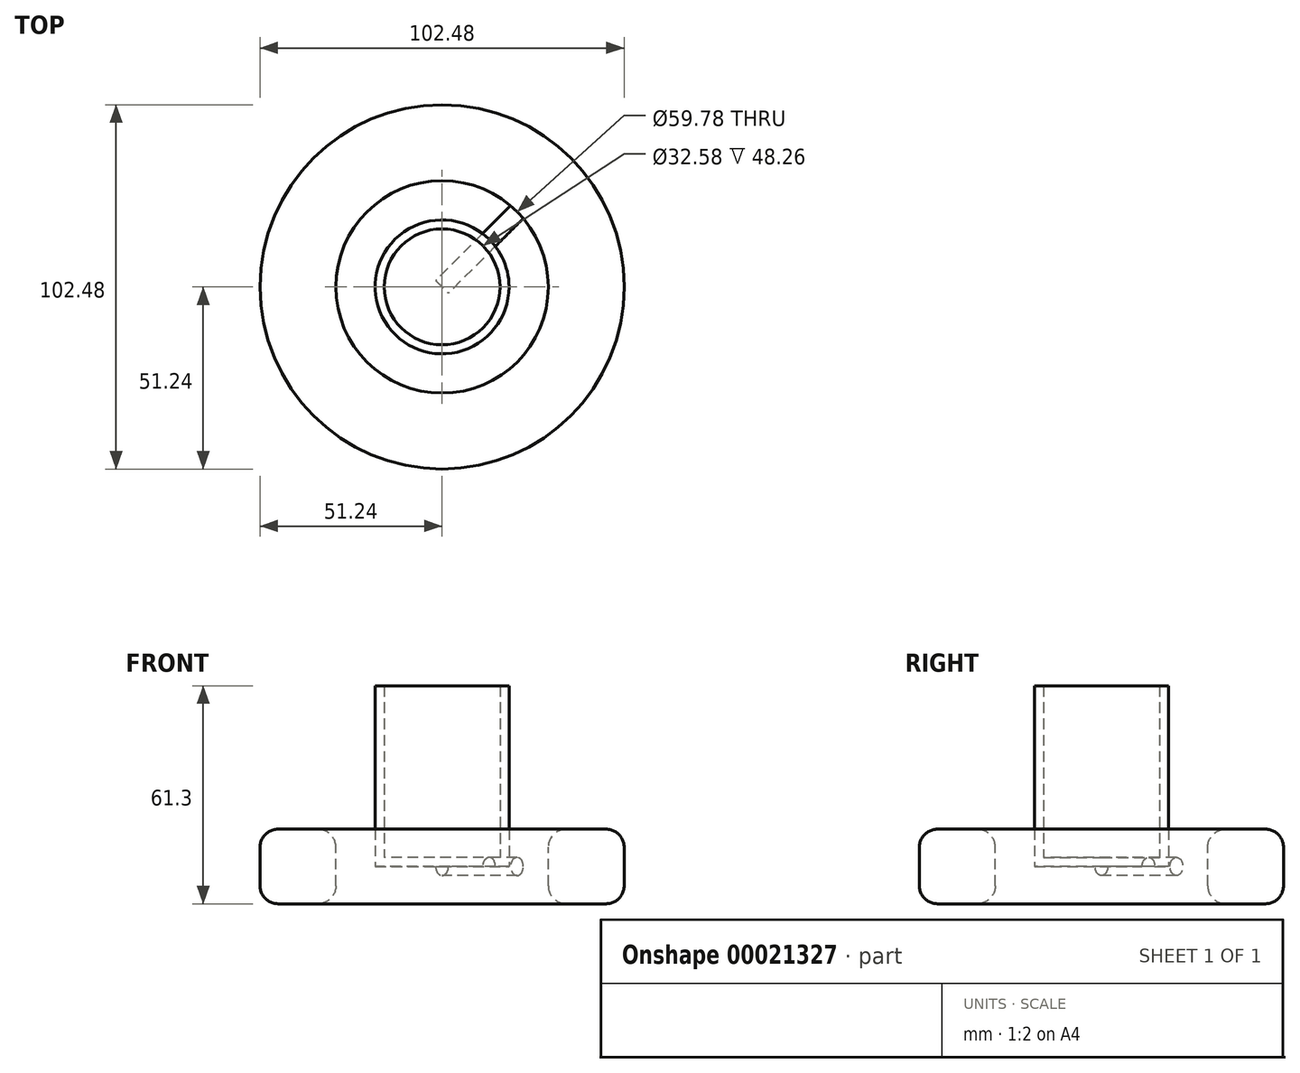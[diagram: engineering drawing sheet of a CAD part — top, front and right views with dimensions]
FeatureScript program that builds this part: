
annotation { "Feature Type Name" : "Feature", "Feature Type Description" : "" }
export const myFeature = defineFeature(function(context is Context, id is Id, definition is map)
    precondition{}
    {
        {
            var Q0;
            Q0=qCreatedBy(makeId("Front.planeOp"),FACE);
            var Q1;
            Q1=qCreatedBy(makeId("Right.planeOp"),FACE);
            cPlane(context, id + "F0", {"entities" : qUnion([Q0, Q1]), "cplaneType" : CPlaneType.MID_PLANE, "offset" : 152.4 * mm, "width" : 152.4 * mm, "height" : 152.4 * mm});
        }
        {
            var Q0;
            Q0=qCreatedBy(makeId("Front.planeOp"),FACE);
            var sketch = newSketch(context, id + "F1", { "sketchPlane" : qUnion([Q0])});
            skLineSegment(sketch, "E0.rect.bottom", {"start": v(-29.89, -10.5) * mm, "end": v(-51.24, -10.5) * mm});
            skLineSegment(sketch, "E0.rect.top", {"start": v(-29.89, 10.5) * mm, "end": v(-51.24, 10.5) * mm});
            skLineSegment(sketch, "E0.rect.left", {"start": v(-29.89, -10.5) * mm, "end": v(-29.89, 10.5) * mm});
            skLineSegment(sketch, "E0.rect.right", {"start": v(-51.24, -10.5) * mm, "end": v(-51.24, 10.5) * mm});
            skPoint(sketch, "E0.rect.middle", {"position": v(-40.56, 0) * mm});
            skSolve(sketch);
        }
        {
            var Q0;
            Q0=qCreatedBy(makeId("Front.planeOp"),FACE);
            var sketch = newSketch(context, id + "F2", { "sketchPlane" : qUnion([Q0])});
            skLineSegment(sketch, "E1", {"start": v(0, 53.18) * mm, "end": v(0, -49.93) * mm});
            skSolve(sketch);
        }
        {
            var Q0;
            Q0=makeQuery(id+"F1.imprint","IMPRINT",FACE,{"disambiguationData":[TD([[makeQuery(id+"F1.imprint","IMPRINT",EDGE,{"derivedFrom":sQuery(id+"F1.wireOp",EDGE,"E0.rect.bottom")}),-1.0]])]});
            var Q1;
            Q1=sQuery(id+"F2.wireOp",EDGE,"E1");
            revolve(context, id + "F3", {"entities" : qUnion([Q0]), "axis" : qUnion([Q1]), "revolveType" : RevolveType.FULL});
        }
        {
            var Q0;
            Q0=makeQuery(id+"F3.opRevolve","SWEPT_FACE",FACE,{"disambiguationData":[OSD([sQuery(id+"F1.wireOp",EDGE,"E0.rect.top")])]});
            fillet(context, id + "F4", {"entities" : qUnion([Q0]), "radius" : 5.08 * mm, "tangentPropagation" : true, "allowEdgeOverflow" : false});
        }
        {
            var Q0;
            Q0=makeQuery(id+"F3.opRevolve","SWEPT_FACE",FACE,{"disambiguationData":[OSD([sQuery(id+"F1.wireOp",EDGE,"E0.rect.bottom")])]});
            fillet(context, id + "F5", {"entities" : qUnion([Q0]), "radius" : 5.08 * mm, "tangentPropagation" : true, "allowEdgeOverflow" : false});
        }
        {
            var Q0;
            Q0=qCreatedBy(makeId("Top.planeOp"),FACE);
            var sketch = newSketch(context, id + "F6", { "sketchPlane" : qUnion([Q0])});
            skCircle(sketch, "E2", {"center": v(0, 0) * mm, "radius": 18.83 * mm});
            skLineSegment(sketch, "E3", {"start": v(0, 0) * mm, "end": v(1955.3, -16.7) * mm});
            skSolve(sketch);
        }
        {
            var Q0;
            Q0=makeQuery(id+"F6.imprint","IMPRINT",FACE,{"disambiguationData":[TD([[makeQuery(id+"F6.imprint","IMPRINT",EDGE,{"derivedFrom":sQuery(id+"F6.wireOp",EDGE,"E2")}),1.0]])]});
            extrude(context, id + "F7", {"entities" : qUnion([Q0]), "depth" : 50.8 * mm});
        }
        {
            var Q0;
            Q0=makeQuery(id+"F7.opExtrude","CAP_FACE",FACE,{"disambiguationData":[OSD([sQuery(id+"F6.wireOp",EDGE,"E2")])],"isStart":false});
            shell(context, id + "F8", {"entities" : qUnion([Q0]), "thickness" : 2.54 * mm});
        }
        {
            var Q0;
            Q0=qCreatedBy(id+"F0.planeOp",FACE);
            var sketch = newSketch(context, id + "F9", { "sketchPlane" : qUnion([Q0])});
            skCircle(sketch, "E4", {"center": v(0, 0) * mm, "radius": 2.54 * mm});
            skSolve(sketch);
        }
        {
            var Q0;
            Q0=sQuery(id+"F9.wireOp",EDGE,"E4");
            extrude(context, id + "F10", {"bodyType" : ToolBodyType.SURFACE, "surfaceEntities" : qUnion([Q0]), "depth" : 30.77 * mm});
        }
        {
            var Q0;
            Q0 = qSketchRegion(id + "F9", true);
            extrude(context, id + "F11", {"entities" : qUnion([Q0]), "operationType" : NewBodyOperationType.ADD, "oppositeDirection" : true, "depth" : 30.95 * mm});
        }
    });
